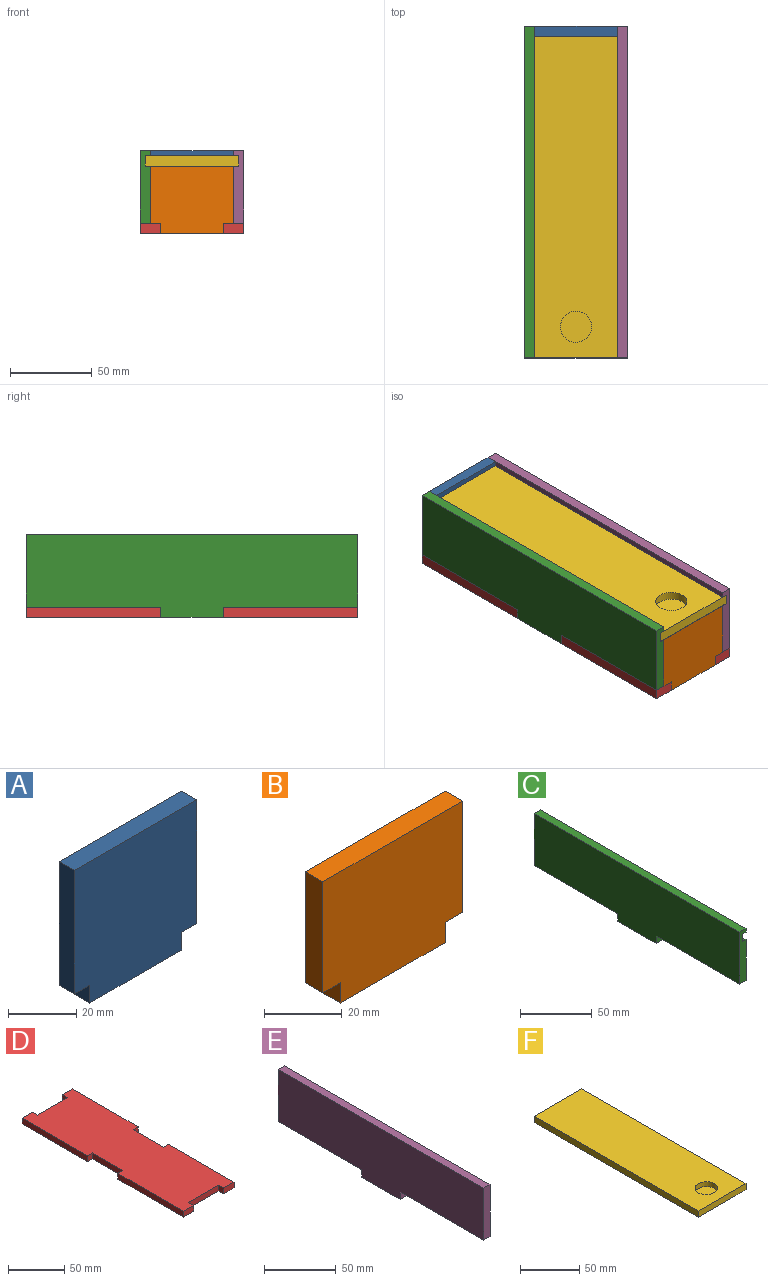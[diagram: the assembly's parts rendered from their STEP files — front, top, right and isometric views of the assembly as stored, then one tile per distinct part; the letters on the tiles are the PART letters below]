
ASSEMBLY  parts=6 mates=5
PART A: 10 faces, bbox 50.8x6.4x50.8 mm
  f0: plane 38.1x6.35mm, normal (0,0,-1), area 241.9mm2, adj f1,f7,f8,f9
  f1: plane 6.35x6.35mm, normal (1,0,0), area 40.3mm2, adj f0,f2,f8,f9
  f2: plane 6.35x6.35mm, normal (0,0,-1), area 40.3mm2, adj f1,f3,f8,f9
  f3: plane 44.45x6.35mm, normal (1,0,0), area 282.3mm2, adj f2,f4,f8,f9
  f4: plane 50.8x6.35mm, normal (0,0,1), area 322.6mm2, adj f3,f5,f8,f9
  f5: plane 44.45x6.35mm, normal (-1,0,0), area 282.3mm2, adj f4,f6,f8,f9
  f6: plane 6.35x6.35mm, normal (0,0,-1), area 40.3mm2, adj f5,f7,f8,f9
  f7: plane 6.35x6.35mm, normal (-1,0,0), area 40.3mm2, adj f0,f6,f8,f9
  f8: plane 50.8x50.8mm, normal (0,-1,0), area 2500mm2, adj f0,f1,f2,f3,f4,f5,f6,f7
  f9: plane 50.8x50.8mm, normal (0,1,0), area 2500mm2, adj f0,f1,f2,f3,f4,f5,f6,f7
PART B: 10 faces, bbox 50.8x6.4x41.3 mm
  f0: plane 38.1x6.35mm, normal (0,0,-1), area 241.9mm2, adj f1,f7,f8,f9
  f1: plane 6.35x6.35mm, normal (1,0,0), area 40.3mm2, adj f0,f2,f8,f9
  f2: plane 6.35x6.35mm, normal (0,0,-1), area 40.3mm2, adj f1,f3,f8,f9
  f3: plane 34.93x6.35mm, normal (1,0,0), area 221.8mm2, adj f2,f4,f8,f9
  f4: plane 50.8x6.35mm, normal (0,0,1), area 322.6mm2, adj f3,f5,f8,f9
  f5: plane 34.93x6.35mm, normal (-1,0,0), area 221.8mm2, adj f4,f6,f8,f9
  f6: plane 6.35x6.35mm, normal (0,0,-1), area 40.3mm2, adj f5,f7,f8,f9
  f7: plane 6.35x6.35mm, normal (-1,0,0), area 40.3mm2, adj f0,f6,f8,f9
  f8: plane 50.8x41.28mm, normal (0,-1,0), area 2016.1mm2, adj f0,f1,f2,f3,f4,f5,f6,f7
  f9: plane 50.8x41.28mm, normal (0,1,0), area 2016.1mm2, adj f0,f1,f2,f3,f4,f5,f6,f7
PART C: 14 faces, bbox 6.4x203.2x50.8 mm
  f0: plane 203.2x50.8mm, normal (1,0,0), area 8024.2mm2, adj f1,f2,f3,f4,f5,f6,f7,f8
  f1: plane 38.1x6.35mm, normal (0,0,-1), area 241.9mm2, adj f0,f2,f8,f9
  f2: plane 6.35x6.35mm, normal (0,1,0), area 40.3mm2, adj f0,f1,f3,f9
  f3: plane 82.55x6.35mm, normal (0,0,-1), area 524.2mm2, adj f0,f2,f4,f9
  f4: plane 44.45x6.35mm, normal (0,1,0), area 282.3mm2, adj f0,f3,f5,f9
  f5: plane 203.2x6.35mm, normal (0,0,1), area 1290.3mm2, adj f0,f4,f6,f9
  f6: plane 44.45x6.35mm, normal (0,-1,0), area 262.1mm2, adj f0,f5,f7,f9,f10,f11,f13
  f7: plane 82.55x6.35mm, normal (0,0,-1), area 524.2mm2, adj f0,f6,f8,f9
  f8: plane 6.35x6.35mm, normal (0,-1,0), area 40.3mm2, adj f0,f1,f7,f9
  f9: plane 203.2x50.8mm, normal (-1,0,0), area 9274.2mm2, adj f1,f2,f3,f4,f5,f6,f7,f8
  f10: plane 196.85x3.18mm, normal (0,0,-1), area 625mm2, adj f0,f6,f12,f13
  f11: plane 196.85x3.18mm, normal (0,0,1), area 625mm2, adj f0,f6,f12,f13
  f12: plane 6.35x3.18mm, normal (0,-1,0), area 20.2mm2, adj f0,f10,f11,f13
  f13: plane 196.85x6.35mm, normal (1,0,0), area 1250mm2, adj f6,f10,f11,f12
PART D: 22 faces, bbox 63.5x203.2x6.4 mm
  f0: plane 38.1x6.35mm, normal (1,0,0), area 241.9mm2, adj f1,f19,f20,f21
  f1: plane 6.35x6.35mm, normal (0,-1,0), area 40.3mm2, adj f0,f2,f20,f21
  f2: plane 82.55x6.35mm, normal (1,0,0), area 524.2mm2, adj f1,f3,f20,f21
  f3: plane 12.7x6.35mm, normal (0,1,0), area 80.6mm2, adj f2,f4,f20,f21
  f4: plane 6.35x6.35mm, normal (-1,0,0), area 40.3mm2, adj f3,f5,f20,f21
  f5: plane 38.1x6.35mm, normal (0,1,0), area 241.9mm2, adj f4,f6,f20,f21
  f6: plane 6.35x6.35mm, normal (1,0,0), area 40.3mm2, adj f5,f7,f20,f21
  f7: plane 12.7x6.35mm, normal (0,1,0), area 80.6mm2, adj f6,f8,f20,f21
  f8: plane 82.55x6.35mm, normal (-1,0,0), area 524.2mm2, adj f7,f9,f20,f21
  f9: plane 6.35x6.35mm, normal (0,-1,0), area 40.3mm2, adj f8,f10,f20,f21
  f10: plane 38.1x6.35mm, normal (-1,0,0), area 241.9mm2, adj f9,f11,f20,f21
  f11: plane 6.35x6.35mm, normal (0,1,0), area 40.3mm2, adj f10,f12,f20,f21
  f12: plane 82.55x6.35mm, normal (-1,0,0), area 524.2mm2, adj f11,f13,f20,f21
  f13: plane 12.7x6.35mm, normal (0,-1,0), area 80.6mm2, adj f12,f14,f20,f21
  f14: plane 6.35x6.35mm, normal (1,0,0), area 40.3mm2, adj f13,f15,f20,f21
  f15: plane 38.1x6.35mm, normal (0,-1,0), area 241.9mm2, adj f14,f16,f20,f21
  f16: plane 6.35x6.35mm, normal (-1,0,0), area 40.3mm2, adj f15,f17,f20,f21
  f17: plane 12.7x6.35mm, normal (0,-1,0), area 80.6mm2, adj f16,f18,f20,f21
  f18: plane 82.55x6.35mm, normal (1,0,0), area 524.2mm2, adj f17,f19,f20,f21
  f19: plane 6.35x6.35mm, normal (0,1,0), area 40.3mm2, adj f0,f18,f20,f21
  f20: plane 203.2x63.5mm, normal (0,0,1), area 11935.5mm2, adj f0,f1,f2,f3,f4,f5,f6,f7
  f21: plane 203.2x63.5mm, normal (0,0,-1), area 11935.5mm2, adj f0,f1,f2,f3,f4,f5,f6,f7
PART E: 14 faces, bbox 6.4x203.2x50.8 mm
  f0: plane 44.45x6.35mm, normal (0,1,0), area 262.1mm2, adj f1,f4,f5,f9,f10,f11,f13
  f1: plane 203.2x50.8mm, normal (1,0,0), area 8024.2mm2, adj f0,f2,f3,f4,f5,f6,f7,f8
  f2: plane 38.1x6.35mm, normal (0,0,-1), area 241.9mm2, adj f1,f3,f8,f9
  f3: plane 6.35x6.35mm, normal (0,1,0), area 40.3mm2, adj f1,f2,f4,f9
  f4: plane 82.55x6.35mm, normal (0,0,-1), area 524.2mm2, adj f0,f1,f3,f9
  f5: plane 203.2x6.35mm, normal (0,0,1), area 1290.3mm2, adj f0,f1,f6,f9
  f6: plane 44.45x6.35mm, normal (0,-1,0), area 282.3mm2, adj f1,f5,f7,f9
  f7: plane 82.55x6.35mm, normal (0,0,-1), area 524.2mm2, adj f1,f6,f8,f9
  f8: plane 6.35x6.35mm, normal (0,-1,0), area 40.3mm2, adj f1,f2,f7,f9
  f9: plane 203.2x50.8mm, normal (-1,0,0), area 9274.2mm2, adj f0,f2,f3,f4,f5,f6,f7,f8
  f10: plane 196.85x3.18mm, normal (0,0,1), area 625mm2, adj f0,f1,f12,f13
  f11: plane 196.85x3.18mm, normal (0,0,-1), area 625mm2, adj f0,f1,f12,f13
  f12: plane 6.35x3.18mm, normal (0,1,0), area 20.2mm2, adj f1,f10,f11,f13
  f13: plane 196.85x6.35mm, normal (1,0,0), area 1250mm2, adj f0,f10,f11,f12
PART F: 8 faces, bbox 57.2x196.9x6.4 mm
  f0: plane 57.15x6.35mm, normal (0,-1,0), area 362.9mm2, adj f1,f3,f4,f5
  f1: plane 196.85x6.35mm, normal (1,0,0), area 1250mm2, adj f0,f2,f4,f5
  f2: plane 57.15x6.35mm, normal (0,1,0), area 362.9mm2, adj f1,f3,f4,f5
  f3: plane 196.85x6.35mm, normal (-1,0,0), area 1250mm2, adj f0,f2,f4,f5
  f4: plane 196.85x57.15mm, normal (0,0,1), area 10965mm2, adj f0,f1,f2,f3,f6
  f5: plane 196.85x57.15mm, normal (0,0,-1), area 11250mm2, adj f0,f1,f2,f3
  f6: cylinder r=9.53mm len=19.05mm, axis (0,0,1), area 304mm2, adj f4,f7
  f7: plane 19.05x19.05mm, normal (0,0,1), area 285mm2, adj f6
PLACE A t=(0,101.6,28.58)mm
PLACE B t=(0,-95.25,23.81)mm
PLACE C t=(-31.75,0,28.58)mm
PLACE D at identity
PLACE E rot(axis=(0,0,1),180deg) t=(31.75,0,28.58)mm
PLACE F t=(0,-3.17,41.28)mm
MATE fastened D.f20 <-> C.f7  axis (0,0,1) through (-31.75,-101.6,6.35)mm
MATE fastened A.f8 <-> D.f5  axis (0,-1,0) through (0,95.25,0)mm
MATE fastened D.f15 <-> B.f9  axis (0,-1,0) through (0,-95.25,0)mm
MATE fastened D.f0 <-> E.f1  axis (1,0,0) through (25.4,0,0)mm
MATE slider A.f8 <-> F.f2  axis (0,-1,0) through (0,95.25,50.8)mm
